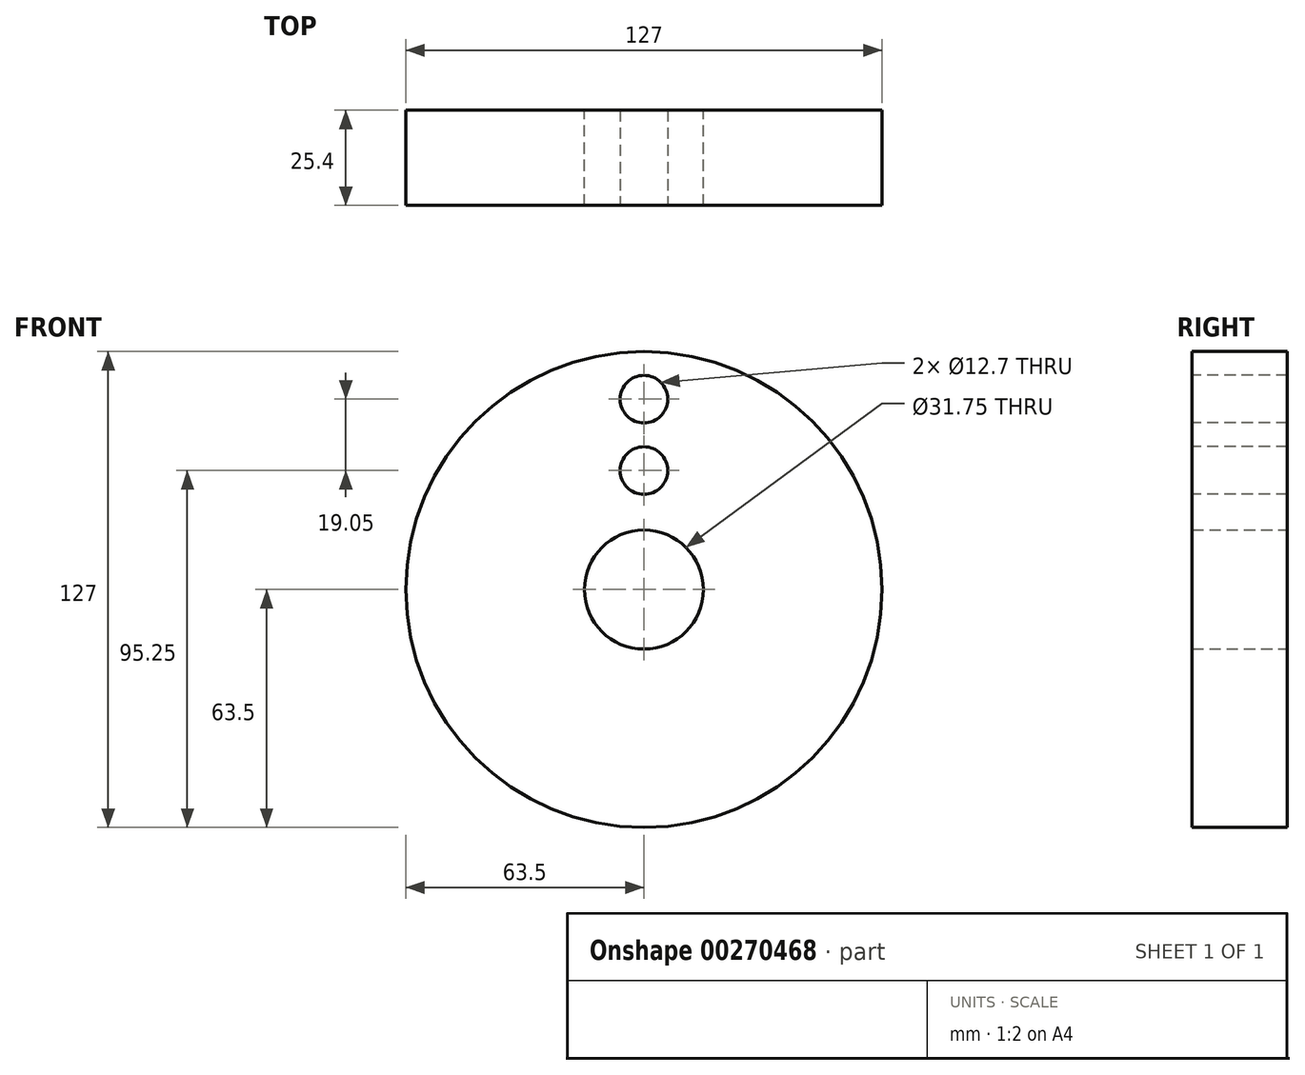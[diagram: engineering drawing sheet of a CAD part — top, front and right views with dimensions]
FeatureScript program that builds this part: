
annotation { "Feature Type Name" : "Feature", "Feature Type Description" : "" }
export const myFeature = defineFeature(function(context is Context, id is Id, definition is map)
    precondition{}
    {
        {
            var Q0;
            Q0=qCreatedBy(makeId("Front.planeOp"),FACE);
            var sketch = newSketch(context, id + "F0", { "sketchPlane" : qUnion([Q0])});
            skCircle(sketch, "E0", {"center": v(0, 0) * mm, "radius": 63.5 * mm});
            skCircle(sketch, "E1", {"center": v(0, 0) * mm, "radius": 15.88 * mm});
            skSolve(sketch);
        }
        {
            var Q0;
            Q0=makeQuery(id+"F0.imprint","IMPRINT",FACE,{"disambiguationData":[TD([[makeQuery(id+"F0.imprint","IMPRINT",EDGE,{"derivedFrom":sQuery(id+"F0.wireOp",EDGE,"E0")}),1.0]])]});
            extrude(context, id + "F1", {"entities" : qUnion([Q0]), "depth" : 25.4 * mm});
        }
        {
            var Q0;
            Q0=makeQuery(id+"F1.opExtrude","CAP_FACE",FACE,{"disambiguationData":[OSD([sQuery(id+"F0.wireOp",EDGE,"E0"),sQuery(id+"F0.wireOp",EDGE,"E1")])],"isStart":false});
            var sketch = newSketch(context, id + "F2", { "sketchPlane" : qUnion([Q0])});
            skCircle(sketch, "E2", {"center": v(0, 50.8) * mm, "radius": 6.35 * mm});
            skCircle(sketch, "E3", {"center": v(0, 31.75) * mm, "radius": 6.35 * mm});
            skSolve(sketch);
        }
        {
            var Q0;
            Q0 = qSketchRegion(id + "F2", true);
            extrude(context, id + "F3", {"entities" : qUnion([Q0]), "operationType" : NewBodyOperationType.REMOVE, "endBound" : BoundingType.UP_TO_NEXT, "oppositeDirection" : true, "depth" : 25.4 * mm});
        }
    });
